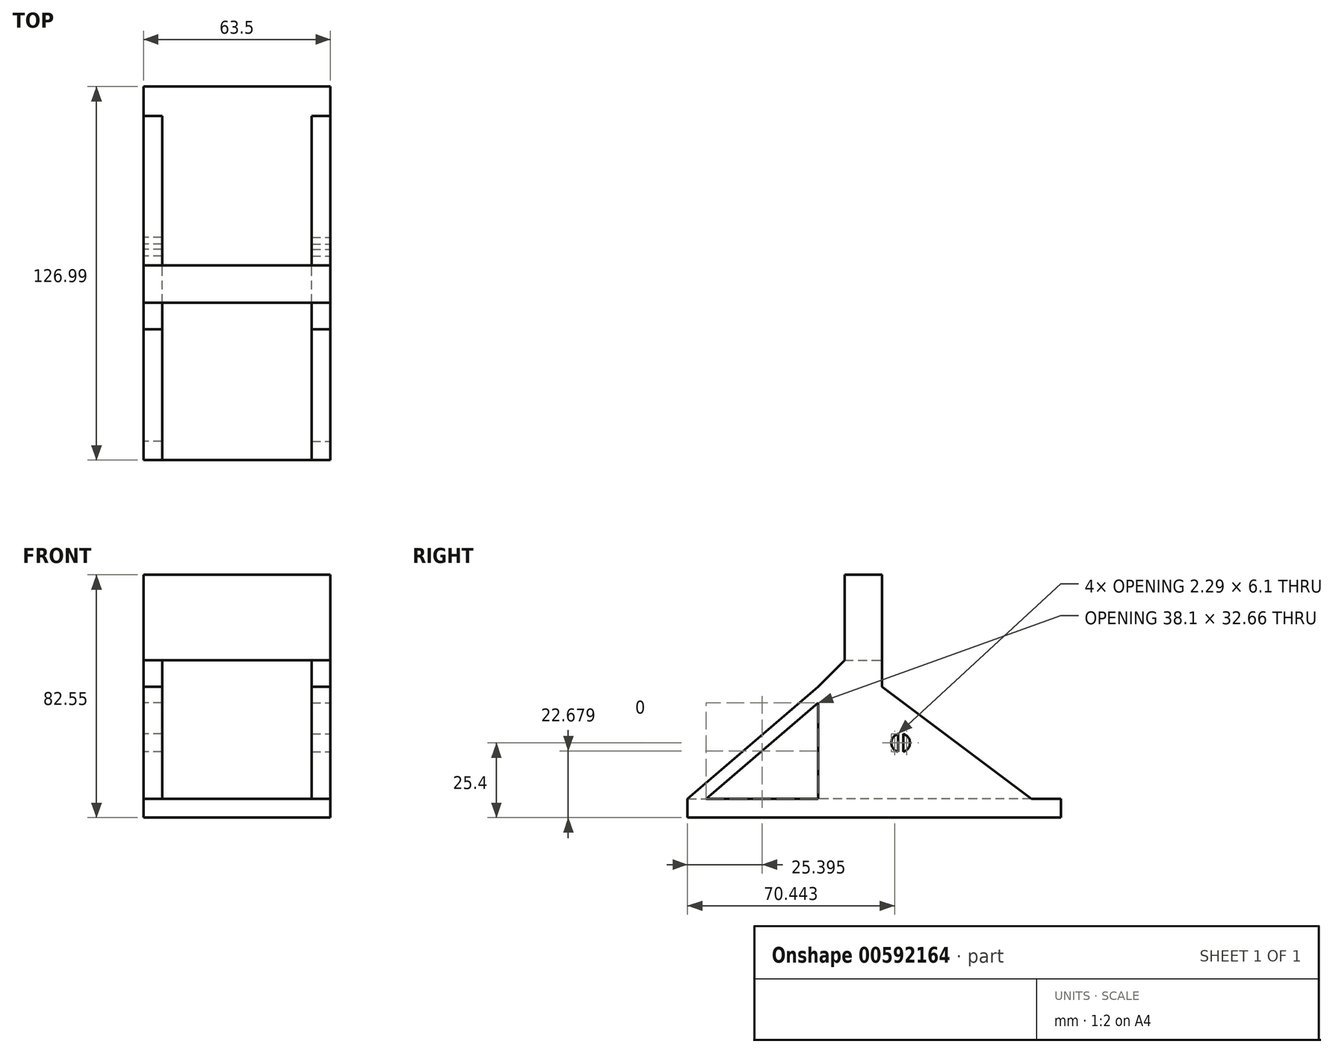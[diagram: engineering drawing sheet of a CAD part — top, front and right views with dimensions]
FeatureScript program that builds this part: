
annotation { "Feature Type Name" : "Feature", "Feature Type Description" : "" }
export const myFeature = defineFeature(function(context is Context, id is Id, definition is map)
    precondition{}
    {
        {
            var Q0;
            Q0=qCreatedBy(makeId("Top.planeOp"),FACE);
            var sketch = newSketch(context, id + "F0", { "sketchPlane" : qUnion([Q0])});
            skLineSegment(sketch, "E0.bottom", {"start": v(0, 41.28) * mm, "end": v(31.75, 41.28) * mm});
            skLineSegment(sketch, "E0.top", {"start": v(0, -41.28) * mm, "end": v(31.75, -41.28) * mm});
            skLineSegment(sketch, "E0.left", {"start": v(0, 41.28) * mm, "end": v(0, -41.28) * mm});
            skLineSegment(sketch, "E0.right", {"start": v(31.75, 41.28) * mm, "end": v(31.75, -41.28) * mm});
            skSolve(sketch);
        }
        {
            var Q0;
            Q0=makeQuery(id+"F0.imprint","IMPRINT",FACE,{"disambiguationData":[TD([[makeQuery(id+"F0.imprint","IMPRINT",EDGE,{"derivedFrom":sQuery(id+"F0.wireOp",EDGE,"E0.bottom")}),-1.0]])]});
            extrude(context, id + "F1", {"entities" : qUnion([Q0]), "depth" : 6.35 * mm, "offsetDistance" : 25.4 * mm});
        }
        {
            var Q0;
            Q0=makeQuery(id+"F1.opExtrude","SWEPT_FACE",FACE,{"disambiguationData":[OSD([sQuery(id+"F0.wireOp",EDGE,"E0.right")])]});
            var sketch = newSketch(context, id + "F2", { "sketchPlane" : qUnion([Q0])});
            skLineSegment(sketch, "E1", {"start": v(-41.28, 6.35) * mm, "end": v(-41.28, 44.45) * mm});
            skLineSegment(sketch, "E2", {"start": v(-41.28, 44.45) * mm, "end": v(-32.3, 53.43) * mm});
            skLineSegment(sketch, "E3", {"start": v(-32.3, 53.43) * mm, "end": v(-32.3, 82.55) * mm});
            skLineSegment(sketch, "E4", {"start": v(-32.3, 82.55) * mm, "end": v(-19.6, 82.55) * mm});
            skLineSegment(sketch, "E5", {"start": v(-19.6, 82.55) * mm, "end": v(-19.6, 44.45) * mm});
            skLineSegment(sketch, "E6", {"start": v(-19.6, 44.45) * mm, "end": v(31.2, 6.35) * mm});
            skLineSegment(sketch, "E7", {"start": v(-32.3, 53.43) * mm, "end": v(-19.6, 53.43) * mm});
            skLineSegment(sketch, "E8", {"start": v(-19.6, 44.45) * mm, "end": v(-19.6, 25.4) * mm, "construction": true});
            skCircle(sketch, "E9", {"center": v(-13.24, 25.4) * mm, "radius": 3.18 * mm});
            skLineSegment(sketch, "E10", {"start": v(-14.13, 28.45) * mm, "end": v(-14.13, 22.35) * mm});
            skLineSegment(sketch, "E11", {"start": v(-12.36, 22.35) * mm, "end": v(-12.36, 28.45) * mm});
            skLineSegment(sketch, "E12", {"start": v(-19.6, 25.4) * mm, "end": v(-13.24, 25.4) * mm, "construction": true});
            skSolve(sketch);
        }
        {
            var Q0;
            {var subQ3=sQuery(id+"F2.wireOp",EDGE,"E1");Q0=makeQuery(id+"F2.imprint","IMPRINT",FACE,{"disambiguationData":[TD([[makeQuery(id+"F2.imprint","IMPRINT",EDGE,{"derivedFrom":subQ3}),-1.0]])]});}
            var Q1;
            {var subQ0=sQuery(id+"F2.wireOp",EDGE,"E10");Q1=makeQuery(id+"F2.imprint","IMPRINT",FACE,{"disambiguationData":[TD([[makeQuery(id+"F2.imprint","IMPRINT",EDGE,{"derivedFrom":subQ0}),1.0]])]});}
            extrude(context, id + "F3", {"entities" : qUnion([Q0, Q1]), "operationType" : NewBodyOperationType.ADD, "oppositeDirection" : true, "depth" : 6.35 * mm, "offsetDistance" : 25.4 * mm});
        }
        {
            var Q0;
            Q0=makeQuery(id+"F2.imprint","IMPRINT",FACE,{"disambiguationData":[TD([[makeQuery(id+"F2.imprint","IMPRINT",EDGE,{"derivedFrom":sQuery(id+"F2.wireOp",EDGE,"E3")}),-1.0]])]});
            extrude(context, id + "F4", {"entities" : qUnion([Q0]), "operationType" : NewBodyOperationType.ADD, "oppositeDirection" : true, "depth" : 31.75 * mm, "offsetDistance" : 25.4 * mm});
        }
        {
            var Q0;
            {var subQ0=makeQuery(id+"F3.boolean.opBoolean","MERGE",FACE,{"derivedFrom":[makeQuery(id+"F1.opExtrude","SWEPT_FACE",FACE,{"disambiguationData":[OSD([sQuery(id+"F0.wireOp",EDGE,"E0.top")])]}),makeQuery(id+"F3.opExtrude","SWEPT_FACE",FACE,{"disambiguationData":[OSD([sQuery(id+"F2.wireOp",EDGE,"E1")])]})]});Q0=makeQuery(id+"F9.boolean.opBoolean","MERGE",FACE,{"derivedFrom":[subQ0,makeQuery(id+"F9.opPattern","COPY",FACE,{"derivedFrom":subQ0,"instanceName":"1"})]});}
            var sketch = newSketch(context, id + "F5", { "sketchPlane" : qUnion([Q0])});
            skLineSegment(sketch, "E13", {"start": v(0, 6.35) * mm, "end": v(31.75, 6.35) * mm});
            skLineSegment(sketch, "E14", {"start": v(31.75, 6.35) * mm, "end": v(31.75, 0) * mm});
            skLineSegment(sketch, "E15", {"start": v(31.75, 0) * mm, "end": v(0, 0) * mm});
            skLineSegment(sketch, "E16", {"start": v(0, 0) * mm, "end": v(0, 6.35) * mm});
            skSolve(sketch);
        }
        {
            var Q0;
            {var subQ0=sQuery(id+"F5.wireOp",EDGE,"E14");Q0=makeQuery(id+"F5.imprint","IMPRINT",FACE,{"disambiguationData":[TD([[makeQuery(id+"F5.imprint","IMPRINT",EDGE,{"derivedFrom":subQ0}),-1.0]])]});}
            extrude(context, id + "F6", {"entities" : qUnion([Q0]), "operationType" : NewBodyOperationType.ADD, "depth" : 44.45 * mm, "offsetDistance" : 25.4 * mm});
        }
        {
            var Q0;
            {var subQ0=sQuery(id+"F2.wireOp",EDGE,"E7");var subQ1=sQuery(id+"F2.wireOp",EDGE,"E5");var subQ2=sQuery(id+"F0.wireOp",EDGE,"E0.right");Q0=makeQuery(id+"F6.boolean.opBoolean","MERGE",FACE,{"derivedFrom":[makeQuery(id+"F4.boolean.opBoolean","MERGE",FACE,{"derivedFrom":[makeQuery(id+"F3.boolean.opBoolean","MERGE",FACE,{"derivedFrom":[makeQuery(id+"F1.opExtrude","SWEPT_FACE",FACE,{"disambiguationData":[OSD([subQ2])]}),makeQuery(id+"F3.opExtrude","CAP_FACE",FACE,{"disambiguationData":[OSD([subQ2,sQuery(id+"F2.wireOp",EDGE,"E1"),sQuery(id+"F2.wireOp",EDGE,"E2"),subQ1,sQuery(id+"F2.wireOp",EDGE,"E6"),subQ0,sQuery(id+"F2.wireOp",EDGE,"E9"),sQuery(id+"F2.wireOp",EDGE,"E10"),sQuery(id+"F2.wireOp",EDGE,"E11")])],"isStart":true})]}),makeQuery(id+"F4.opExtrude","CAP_FACE",FACE,{"disambiguationData":[OSD([sQuery(id+"F2.wireOp",EDGE,"E3"),sQuery(id+"F2.wireOp",EDGE,"E4"),subQ1,subQ0])],"isStart":true})]}),makeQuery(id+"F6.opExtrude","SWEPT_FACE",FACE,{"disambiguationData":[OSD([sQuery(id+"F5.wireOp",EDGE,"E14")])]})]});}
            var sketch = newSketch(context, id + "F7", { "sketchPlane" : qUnion([Q0])});
            skLineSegment(sketch, "E17", {"start": v(-85.73, 6.35) * mm, "end": v(-41.28, 44.45) * mm});
            skLineSegment(sketch, "E18", {"start": v(-85.73, 6.35) * mm, "end": v(-79.38, 6.35) * mm});
            skLineSegment(sketch, "E19", {"start": v(-79.38, 6.35) * mm, "end": v(-41.28, 39) * mm});
            skSolve(sketch);
        }
        {
            var Q0;
            {var subQ0=sQuery(id+"F7.wireOp",EDGE,"E17");Q0=makeQuery(id+"F7.imprint","IMPRINT",FACE,{"disambiguationData":[TD([[makeQuery(id+"F7.imprint","IMPRINT",EDGE,{"derivedFrom":subQ0}),-1.0]])]});}
            extrude(context, id + "F8", {"entities" : qUnion([Q0]), "operationType" : NewBodyOperationType.ADD, "oppositeDirection" : true, "depth" : 6.35 * mm, "offsetDistance" : 25.4 * mm});
        }
        {
            var Q0;
            Q0=makeQuery(id+"F1.opExtrude","SWEPT_BODY",BODY,{"disambiguationData":[OSD([sQuery(id+"F0.wireOp",EDGE,"E0.bottom"),sQuery(id+"F0.wireOp",EDGE,"E0.top"),sQuery(id+"F0.wireOp",EDGE,"E0.left"),sQuery(id+"F0.wireOp",EDGE,"E0.right")])]});
            var Q1;
            Q1=qCreatedBy(makeId("Right.planeOp"),FACE);
            mirror(context, id + "F9", {"operationType" : NewBodyOperationType.ADD, "entities" : qUnion([Q0]), "mirrorPlane" : qUnion([Q1])});
        }
    });
